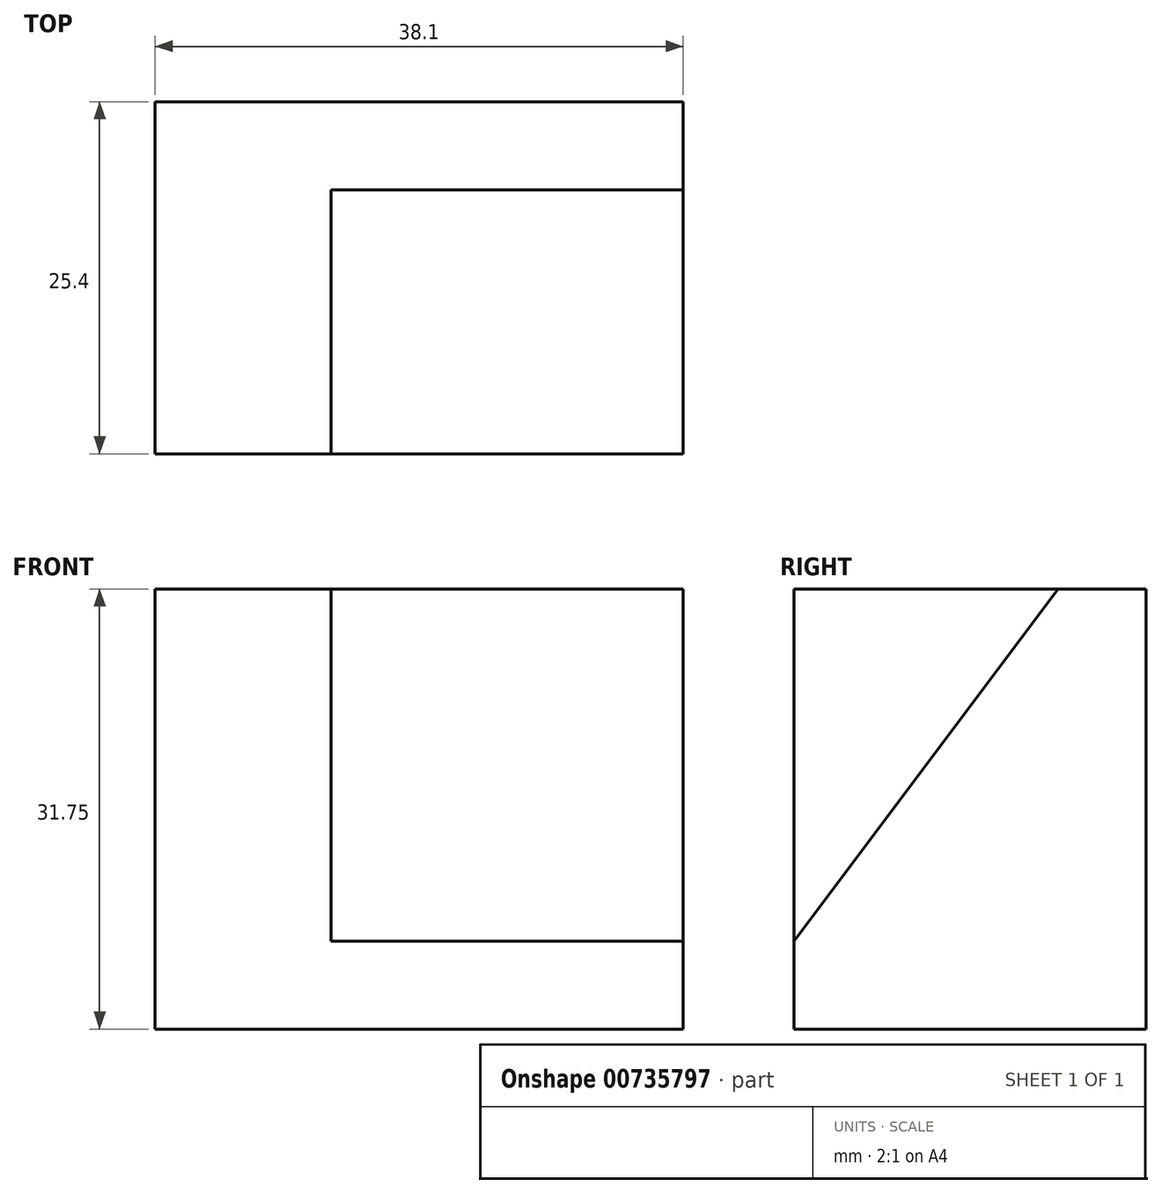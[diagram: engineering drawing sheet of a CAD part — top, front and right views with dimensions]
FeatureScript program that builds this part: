
annotation { "Feature Type Name" : "Feature", "Feature Type Description" : "" }
export const myFeature = defineFeature(function(context is Context, id is Id, definition is map)
    precondition{}
    {
        {
            var Q0;
            Q0=qCreatedBy(makeId("Front.planeOp"),FACE);
            var sketch = newSketch(context, id + "F0", { "sketchPlane" : qUnion([Q0])});
            skLineSegment(sketch, "E0", {"start": v(0, 0) * mm, "end": v(38.1, 0) * mm});
            skLineSegment(sketch, "E1", {"start": v(38.1, 0) * mm, "end": v(38.1, 31.75) * mm});
            skLineSegment(sketch, "E2", {"start": v(38.1, 31.75) * mm, "end": v(0, 31.75) * mm});
            skLineSegment(sketch, "E3", {"start": v(0, 31.75) * mm, "end": v(0, 0) * mm});
            skSolve(sketch);
        }
        {
            var Q0;
            Q0=makeQuery(id+"F0.imprint","IMPRINT",FACE,{"disambiguationData":[TD([[makeQuery(id+"F0.imprint","IMPRINT",EDGE,{"derivedFrom":sQuery(id+"F0.wireOp",EDGE,"E0")}),1.0]])]});
            extrude(context, id + "F1", {"entities" : qUnion([Q0]), "oppositeDirection" : true, "depth" : 25.4 * mm, "offsetDistance" : 25.4 * mm});
        }
        {
            var Q0;
            Q0=makeQuery(id+"F1.opExtrude","CAP_FACE",FACE,{"disambiguationData":[OSD([sQuery(id+"F0.wireOp",EDGE,"E0"),sQuery(id+"F0.wireOp",EDGE,"E1"),sQuery(id+"F0.wireOp",EDGE,"E2"),sQuery(id+"F0.wireOp",EDGE,"E3")])],"isStart":true});
            var sketch = newSketch(context, id + "F2", { "sketchPlane" : qUnion([Q0])});
            skLineSegment(sketch, "E4", {"start": v(12.7, 31.75) * mm, "end": v(12.7, 6.35) * mm});
            skLineSegment(sketch, "E5", {"start": v(12.7, 6.35) * mm, "end": v(38.1, 6.35) * mm});
            skLineSegment(sketch, "E6", {"start": v(38.1, 6.35) * mm, "end": v(38.1, 31.75) * mm});
            skLineSegment(sketch, "E7", {"start": v(38.1, 31.75) * mm, "end": v(12.7, 31.75) * mm});
            skSolve(sketch);
        }
        {
            var Q0;
            Q0=makeQuery(id+"F2.imprint","IMPRINT",FACE,{"disambiguationData":[TD([[makeQuery(id+"F2.imprint","IMPRINT",EDGE,{"derivedFrom":sQuery(id+"F2.wireOp",EDGE,"E4")}),1.0]])]});
            extrude(context, id + "F3", {"entities" : qUnion([Q0]), "operationType" : NewBodyOperationType.REMOVE, "oppositeDirection" : true, "depth" : 19.05 * mm, "offsetDistance" : 25.4 * mm});
        }
        {
            var Q0;
            Q0=makeQuery(id+"F3.boolean.opBoolean","COPY",FACE,{"derivedFrom":makeQuery(id+"F3.opExtrude","SWEPT_FACE",FACE,{"disambiguationData":[OSD([sQuery(id+"F2.wireOp",EDGE,"E4")])]})});
            var sketch = newSketch(context, id + "F4", { "sketchPlane" : qUnion([Q0])});
            skLineSegment(sketch, "E8", {"start": v(0, 6.35) * mm, "end": v(19.05, 6.35) * mm});
            skLineSegment(sketch, "E9", {"start": v(19.05, 6.35) * mm, "end": v(19.05, 31.75) * mm});
            skLineSegment(sketch, "E10", {"start": v(19.05, 31.75) * mm, "end": v(0, 6.35) * mm});
            skSolve(sketch);
        }
        {
            var Q0;
            Q0=makeQuery(id+"F4.imprint","IMPRINT",FACE,{"disambiguationData":[TD([[makeQuery(id+"F4.imprint","IMPRINT",EDGE,{"derivedFrom":sQuery(id+"F4.wireOp",EDGE,"E8")}),-1.0]])]});
            extrude(context, id + "F5", {"entities" : qUnion([Q0]), "operationType" : NewBodyOperationType.ADD, "depth" : 25.4 * mm, "offsetDistance" : 25.4 * mm});
        }
    });
